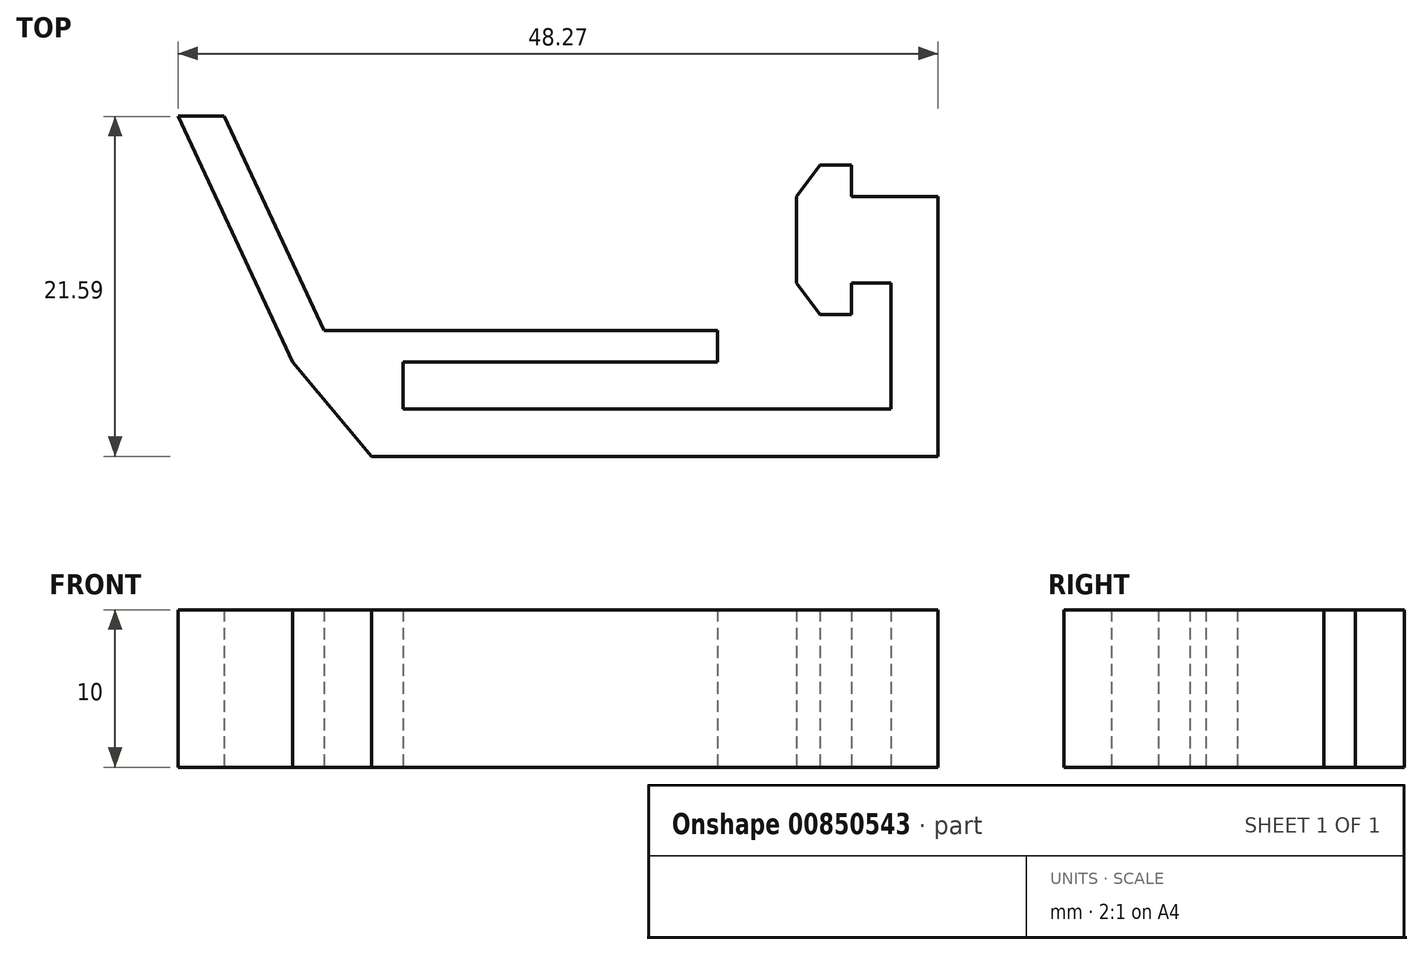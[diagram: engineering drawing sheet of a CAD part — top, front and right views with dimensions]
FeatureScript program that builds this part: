
annotation { "Feature Type Name" : "Feature", "Feature Type Description" : "" }
export const myFeature = defineFeature(function(context is Context, id is Id, definition is map)
    precondition{}
    {
        {
            var Q0;
            Q0=qCreatedBy(makeId("Top.planeOp"),FACE);
            var sketch = newSketch(context, id + "F0", { "sketchPlane" : qUnion([Q0])});
            skLineSegment(sketch, "E0.bottom", {"start": v(14.04, -2.4) * mm, "end": v(16.54, -2.4) * mm});
            skLineSegment(sketch, "E0.top", {"start": v(14.04, 3.1) * mm, "end": v(16.54, 3.1) * mm});
            skLineSegment(sketch, "E0.left", {"start": v(14.04, -2.4) * mm, "end": v(14.04, 3.1) * mm, "construction": true});
            skLineSegment(sketch, "E0.right", {"start": v(16.54, -2.4) * mm, "end": v(16.54, 3.1) * mm, "construction": true});
            skLineSegment(sketch, "E1.bottom", {"start": v(14.04, 3.1) * mm, "end": v(10.54, 3.1) * mm, "construction": true});
            skLineSegment(sketch, "E1.top", {"start": v(14.04, -2.4) * mm, "end": v(10.54, -2.4) * mm, "construction": true});
            skLineSegment(sketch, "E1.left", {"start": v(14.04, 3.1) * mm, "end": v(14.04, -2.4) * mm, "construction": true});
            skLineSegment(sketch, "E1.right", {"start": v(10.54, 3.1) * mm, "end": v(10.54, -2.4) * mm});
            skLineSegment(sketch, "E2.bottom", {"start": v(16.54, 3.1) * mm, "end": v(19.54, 3.1) * mm});
            skLineSegment(sketch, "E2.top", {"start": v(16.54, -2.4) * mm, "end": v(19.54, -2.4) * mm, "construction": true});
            skLineSegment(sketch, "E2.left", {"start": v(16.54, 3.1) * mm, "end": v(16.54, -2.4) * mm, "construction": true});
            skLineSegment(sketch, "E2.right", {"start": v(19.54, 3.1) * mm, "end": v(19.54, -2.4) * mm});
            skLineSegment(sketch, "E3.top", {"start": v(16.54, -10.4) * mm, "end": v(19.54, -10.4) * mm, "construction": true});
            skLineSegment(sketch, "E3.left", {"start": v(16.54, -2.4) * mm, "end": v(16.54, -10.4) * mm});
            skLineSegment(sketch, "E3.right", {"start": v(19.54, -2.4) * mm, "end": v(19.54, -10.4) * mm});
            skLineSegment(sketch, "E4.top", {"start": v(16.54, -13.4) * mm, "end": v(19.54, -13.4) * mm});
            skLineSegment(sketch, "E4.left", {"start": v(16.54, -10.4) * mm, "end": v(16.54, -13.4) * mm, "construction": true});
            skLineSegment(sketch, "E4.right", {"start": v(19.54, -10.4) * mm, "end": v(19.54, -13.4) * mm});
            skLineSegment(sketch, "E5.bottom", {"start": v(16.54, -10.4) * mm, "end": v(-14.46, -10.4) * mm});
            skLineSegment(sketch, "E5.top", {"start": v(16.54, -13.4) * mm, "end": v(-14.46, -13.4) * mm});
            skLineSegment(sketch, "E5.right", {"start": v(-14.46, -10.4) * mm, "end": v(-14.46, -13.4) * mm, "construction": true});
            skLineSegment(sketch, "E6.bottom", {"start": v(-14.46, -13.4) * mm, "end": v(-16.46, -13.4) * mm});
            skLineSegment(sketch, "E6.top", {"start": v(-14.46, -10.4) * mm, "end": v(-16.46, -10.4) * mm, "construction": true});
            skLineSegment(sketch, "E6.left", {"start": v(-14.46, -13.4) * mm, "end": v(-14.46, -10.4) * mm, "construction": true});
            skLineSegment(sketch, "E6.right", {"start": v(-16.46, -13.4) * mm, "end": v(-16.46, -10.4) * mm, "construction": true});
            skLineSegment(sketch, "E7.bottom", {"start": v(-16.46, -10.4) * mm, "end": v(-14.46, -10.4) * mm, "construction": true});
            skLineSegment(sketch, "E7.top", {"start": v(-16.46, -7.4) * mm, "end": v(-14.46, -7.4) * mm, "construction": true});
            skLineSegment(sketch, "E7.left", {"start": v(-16.46, -10.4) * mm, "end": v(-16.46, -7.4) * mm, "construction": true});
            skLineSegment(sketch, "E7.right", {"start": v(-14.46, -10.4) * mm, "end": v(-14.46, -7.4) * mm});
            skLineSegment(sketch, "E8.top", {"start": v(-16.46, -5.4) * mm, "end": v(-14.46, -5.4) * mm});
            skLineSegment(sketch, "E8.left", {"start": v(-16.46, -7.4) * mm, "end": v(-16.46, -5.4) * mm, "construction": true});
            skLineSegment(sketch, "E8.right", {"start": v(-14.46, -7.4) * mm, "end": v(-14.46, -5.4) * mm, "construction": true});
            skLineSegment(sketch, "E9.bottom", {"start": v(-14.46, -5.4) * mm, "end": v(5.54, -5.4) * mm});
            skLineSegment(sketch, "E9.top", {"start": v(-14.46, -7.4) * mm, "end": v(5.54, -7.4) * mm});
            skLineSegment(sketch, "E9.left", {"start": v(-14.46, -5.4) * mm, "end": v(-14.46, -7.4) * mm, "construction": true});
            skLineSegment(sketch, "E9.right", {"start": v(5.54, -5.4) * mm, "end": v(5.54, -7.4) * mm});
            skLineSegment(sketch, "E10.bottom", {"start": v(-16.46, -5.4) * mm, "end": v(-19.46, -5.4) * mm});
            skLineSegment(sketch, "E10.top", {"start": v(-16.46, -7.4) * mm, "end": v(-19.46, -7.4) * mm, "construction": true});
            skLineSegment(sketch, "E10.left", {"start": v(-16.46, -5.4) * mm, "end": v(-16.46, -7.4) * mm, "construction": true});
            skLineSegment(sketch, "E10.right", {"start": v(-19.46, -5.4) * mm, "end": v(-19.46, -7.4) * mm, "construction": true});
            skLineSegment(sketch, "E11.bottom", {"start": v(-19.46, -5.4) * mm, "end": v(-21.46, -5.4) * mm, "construction": true});
            skLineSegment(sketch, "E11.top", {"start": v(-19.46, -7.4) * mm, "end": v(-21.46, -7.4) * mm, "construction": true});
            skLineSegment(sketch, "E11.right", {"start": v(-21.46, -5.4) * mm, "end": v(-21.46, -7.4) * mm});
            skLineSegment(sketch, "E12", {"start": v(-21.46, -7.4) * mm, "end": v(-16.46, -13.4) * mm});
            skLineSegment(sketch, "E13.bottom", {"start": v(-21.46, -5.4) * mm, "end": v(-19.46, -5.4) * mm, "construction": true});
            skLineSegment(sketch, "E14.bottom", {"start": v(14.04, 3.1) * mm, "end": v(12.04, 3.1) * mm, "construction": true});
            skLineSegment(sketch, "E14.top", {"start": v(14.04, 5.1) * mm, "end": v(12.04, 5.1) * mm});
            skLineSegment(sketch, "E14.left", {"start": v(14.04, 3.1) * mm, "end": v(14.04, 5.1) * mm});
            skLineSegment(sketch, "E14.right", {"start": v(12.04, 3.1) * mm, "end": v(12.04, 5.1) * mm, "construction": true});
            skLineSegment(sketch, "E15.bottom", {"start": v(14.04, -2.4) * mm, "end": v(12.04, -2.4) * mm, "construction": true});
            skLineSegment(sketch, "E15.top", {"start": v(14.04, -4.4) * mm, "end": v(12.04, -4.4) * mm});
            skLineSegment(sketch, "E15.left", {"start": v(14.04, -2.4) * mm, "end": v(14.04, -4.4) * mm});
            skLineSegment(sketch, "E15.right", {"start": v(12.04, -2.4) * mm, "end": v(12.04, -4.4) * mm, "construction": true});
            skLineSegment(sketch, "E16", {"start": v(10.54, 3.1) * mm, "end": v(12.04, 5.1) * mm});
            skLineSegment(sketch, "E17", {"start": v(10.54, -2.4) * mm, "end": v(12.04, -4.4) * mm});
            skLineSegment(sketch, "E18", {"start": v(-21.46, -5.4) * mm, "end": v(-27.8, 8.2) * mm, "construction": true});
            skLineSegment(sketch, "E19", {"start": v(-19.46, -5.4) * mm, "end": v(-25.8, 8.2) * mm});
            skLineSegment(sketch, "E20", {"start": v(-21.46, -7.4) * mm, "end": v(-28.73, 8.2) * mm});
            skLineSegment(sketch, "E21", {"start": v(-28.73, 8.2) * mm, "end": v(-25.8, 8.2) * mm});
            skSolve(sketch);
        }
        {
            var Q0;
            Q0 = qSketchRegion(id + "F0", true);
            extrude(context, id + "F1", {"entities" : qUnion([Q0]), "depth" : 10 * mm, "offsetDistance" : 25 * mm});
        }
    });
